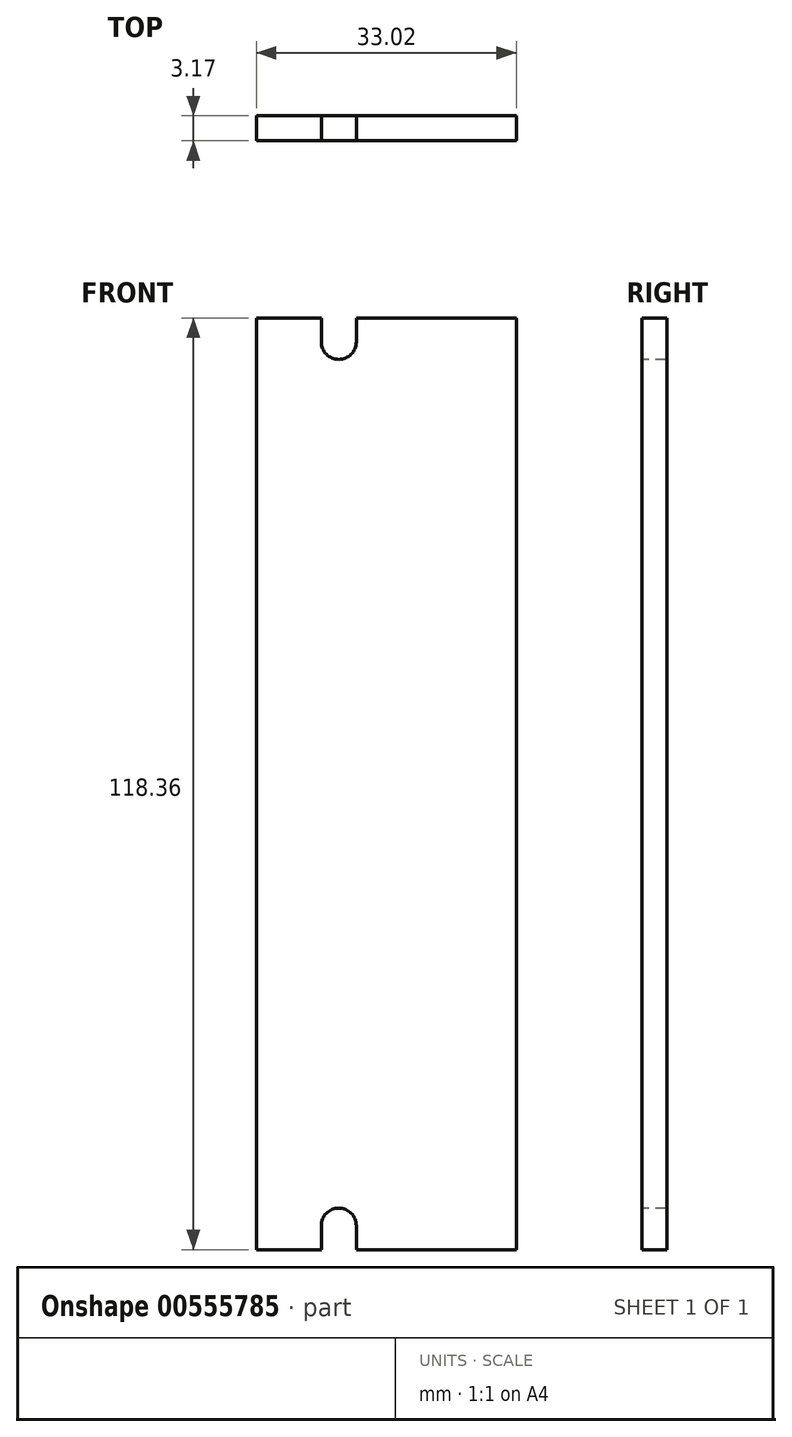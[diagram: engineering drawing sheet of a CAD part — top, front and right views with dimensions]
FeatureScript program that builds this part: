
annotation { "Feature Type Name" : "Feature", "Feature Type Description" : "" }
export const myFeature = defineFeature(function(context is Context, id is Id, definition is map)
    precondition{}
    {
        {
            var Q0;
            Q0=qCreatedBy(makeId("Front.planeOp"),FACE);
            var sketch = newSketch(context, id + "F0", { "sketchPlane" : qUnion([Q0])});
            skLineSegment(sketch, "E0.bottom", {"start": v(0, 0) * mm, "end": v(-33.02, 0) * mm});
            skLineSegment(sketch, "E0.top", {"start": v(0, 118.36) * mm, "end": v(-33.02, 118.36) * mm});
            skLineSegment(sketch, "E0.left", {"start": v(0, 0) * mm, "end": v(0, 118.36) * mm});
            skLineSegment(sketch, "E0.right", {"start": v(-33.02, 0) * mm, "end": v(-33.02, 118.36) * mm});
            skSolve(sketch);
        }
        {
            var Q0;
            Q0 = qSketchRegion(id + "F0", true);
            extrude(context, id + "F1", {"entities" : qUnion([Q0]), "depth" : 3.17 * mm, "offsetDistance" : 25.4 * mm});
        }
        {
            var Q0;
            Q0=makeQuery(id+"F1.opExtrude","CAP_FACE",FACE,{"disambiguationData":[OSD([sQuery(id+"F0.wireOp",EDGE,"E0.bottom"),sQuery(id+"F0.wireOp",EDGE,"E0.top"),sQuery(id+"F0.wireOp",EDGE,"E0.left"),sQuery(id+"F0.wireOp",EDGE,"E0.right")])],"isStart":false});
            var sketch = newSketch(context, id + "F2", { "sketchPlane" : qUnion([Q0])});
            skPoint(sketch, "E1", {"position": v(-22.54, 115.32) * mm});
            skPoint(sketch, "E2", {"position": v(-22.54, 3.05) * mm});
            skArc(sketch, "E3", {"start": v(-24.77, 115.32) * mm, "mid": v(-22.54, 113.1) * mm, "end": v(-20.32, 115.32) * mm});
            skLineSegment(sketch, "E4", {"start": v(-20.32, 115.32) * mm, "end": v(-20.32, 118.36) * mm});
            skLineSegment(sketch, "E5", {"start": v(-24.77, 115.32) * mm, "end": v(-24.77, 118.36) * mm});
            skLineSegment(sketch, "E6", {"start": v(-24.77, 118.36) * mm, "end": v(-20.32, 118.36) * mm});
            skLineSegment(sketch, "E7", {"start": v(-33.02, 59.18) * mm, "end": v(0, 59.18) * mm, "construction": true});
            skLineSegment(sketch, "E8.MirrorCS", {"start": v(-24.76, 3.05) * mm, "end": v(-24.76, 0) * mm});
            skLineSegment(sketch, "E9.MirrorCS", {"start": v(-20.32, 3.05) * mm, "end": v(-20.32, 0) * mm});
            skArc(sketch, "E10.MirrorCS", {"start": v(-24.76, 3.05) * mm, "mid": v(-22.54, 5.27) * mm, "end": v(-20.32, 3.05) * mm});
            skSolve(sketch);
        }
        {
            var Q0;
            {var subQ0=sQuery(id+"F2.wireOp",EDGE,"E8.MirrorCS");Q0=makeQuery(id+"F2.imprint","IMPRINT",FACE,{"disambiguationData":[TD([[makeQuery(id+"F2.imprint","IMPRINT",EDGE,{"derivedFrom":subQ0}),1.0]])]});}
            var Q1;
            Q1=makeQuery(id+"F2.imprint","IMPRINT",FACE,{"disambiguationData":[TD([[makeQuery(id+"F2.imprint","IMPRINT",EDGE,{"derivedFrom":sQuery(id+"F2.wireOp",EDGE,"E3")}),1.0]])]});
            extrude(context, id + "F3", {"entities" : qUnion([Q0, Q1]), "operationType" : NewBodyOperationType.REMOVE, "endBound" : BoundingType.THROUGH_ALL, "oppositeDirection" : true, "depth" : 25.4 * mm, "offsetDistance" : 25.4 * mm});
        }
    });
